# Revit family: Woodfold-Accordion-Door-Family-Series-440-Double
name_source: partatom
category: Doors
units: mm (PartAtom-declared; Revit-internal decimal feet)

## family parameters
Always vertical = Yes
Cut with Voids When Loaded = No
Host = Wall
Room Calculation Point = No
Shared = No

## types (2) — shared parameters
Description = Visifold, see-through commercial security door
Frame Projection Ext. = 0' - 1"
Frame Projection Int. = 0' - 1"
Frame Visibility = Yes
Frame Width = 0' - 3"
Function = Interior
Height = 8' - 0"
Lead Post = Metal - Aluminum
Manufacturer = Woodfold Mfg., Inc.
Model = 440
Panel Connectors = Flexible Vinyl
Panel Material = Woodfold - Acrylic - Clear
Recessed Track = No
Stack Dimension = 1' - 3 1/2"
Surface Track = Yes
Track Material = Metal - Aluminum
Type Comments = Width: No limitation.  Height: Up to 10'-1"
Wall Closure = By host
Width = 8' - 0"

## per-type parameters (varying)
| type | Hardware Type |
| 8'-0" x 8'-0" Surface Mounted w/Deadlatch | Deadlatch with Thumbturn Two-side |
| 8'-0" x 8'-0" Surface Mounted w/Magnetic Catch & Strike Plate | Magnetic Catch & Strike Plate |

## geometry (parser evidence)
native form markers: Sweep x19
no freeform markers — native parametric forms only
